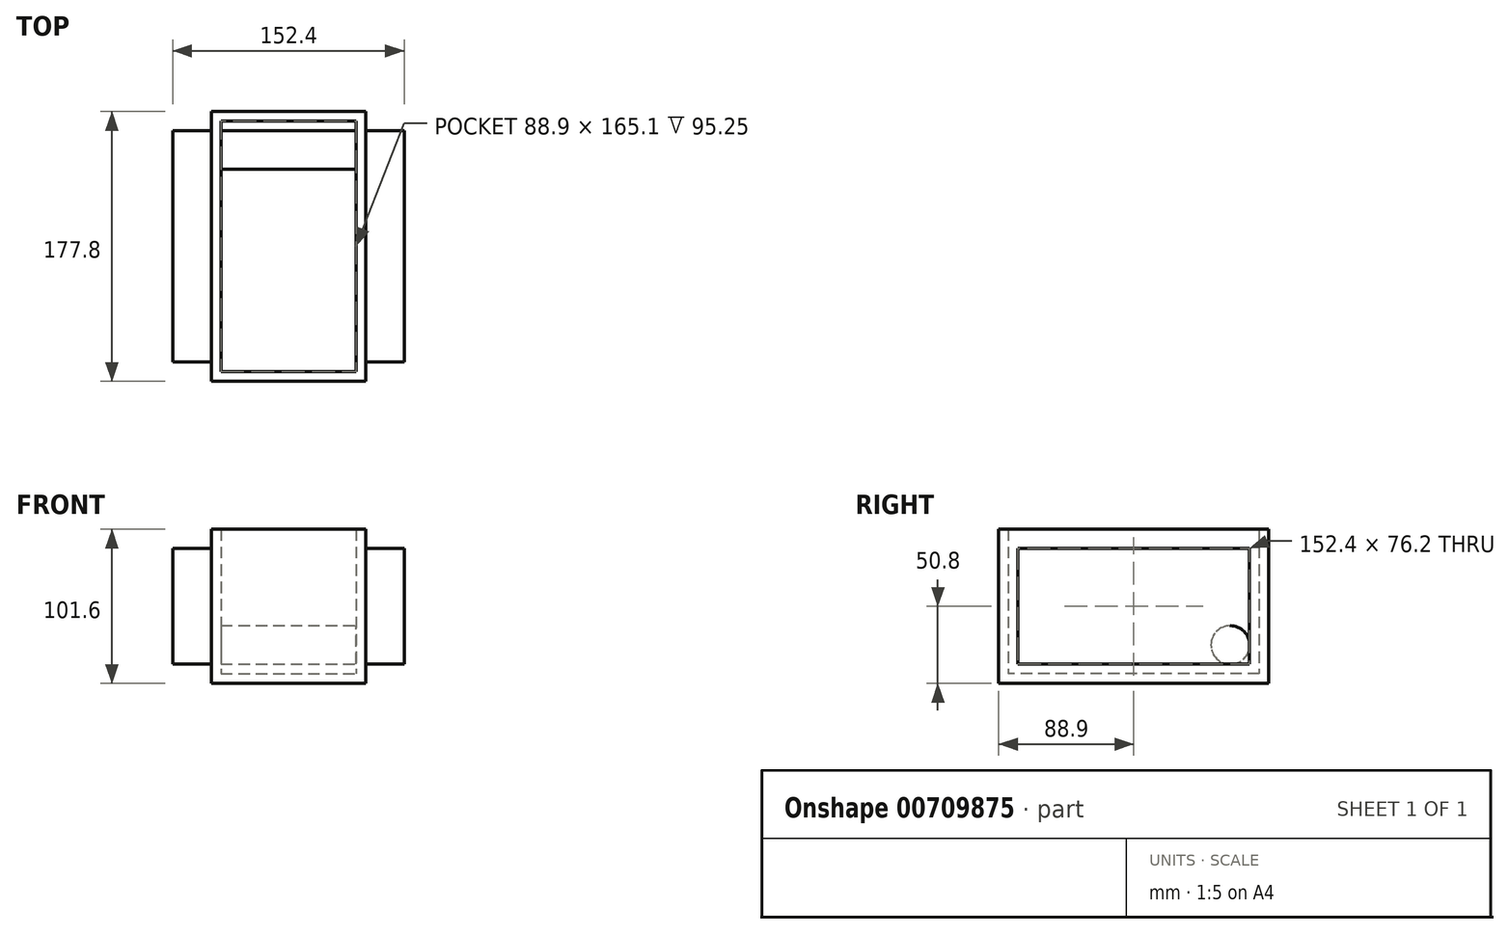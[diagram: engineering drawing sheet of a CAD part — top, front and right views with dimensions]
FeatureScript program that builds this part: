
annotation { "Feature Type Name" : "Feature", "Feature Type Description" : "" }
export const myFeature = defineFeature(function(context is Context, id is Id, definition is map)
    precondition{}
    {
        {
            var Q0;
            Q0=qCreatedBy(makeId("Top.planeOp"),FACE);
            var sketch = newSketch(context, id + "F0", { "sketchPlane" : qUnion([Q0])});
            skLineSegment(sketch, "E0.bottom", {"start": v(-50.8, 88.9) * mm, "end": v(50.8, 88.9) * mm});
            skLineSegment(sketch, "E0.top", {"start": v(-50.8, -88.9) * mm, "end": v(50.8, -88.9) * mm});
            skLineSegment(sketch, "E0.left", {"start": v(-50.8, 88.9) * mm, "end": v(-50.8, -88.9) * mm});
            skLineSegment(sketch, "E0.right", {"start": v(50.8, 88.9) * mm, "end": v(50.8, -88.9) * mm});
            skSolve(sketch);
        }
        {
            var Q0;
            Q0=makeQuery(id+"F0.imprint","IMPRINT",FACE,{"disambiguationData":[TD([[makeQuery(id+"F0.imprint","IMPRINT",EDGE,{"derivedFrom":sQuery(id+"F0.wireOp",EDGE,"E0.bottom")}),-1.0]])]});
            extrude(context, id + "F1", {"entities" : qUnion([Q0]), "endBound" : BoundingType.SYMMETRIC, "depth" : 101.6 * mm, "offsetDistance" : 25.4 * mm});
        }
        {
            var Q0;
            Q0=makeQuery(id+"F1.opExtrude","CAP_FACE",FACE,{"disambiguationData":[OSD([sQuery(id+"F0.wireOp",EDGE,"E0.bottom"),sQuery(id+"F0.wireOp",EDGE,"E0.top"),sQuery(id+"F0.wireOp",EDGE,"E0.left"),sQuery(id+"F0.wireOp",EDGE,"E0.right")])],"isStart":false});
            shell(context, id + "F2", {"entities" : qUnion([Q0]), "thickness" : 6.35 * mm});
        }
        {
            var Q0;
            Q0=makeQuery(id+"F1.opExtrude","SWEPT_FACE",FACE,{"disambiguationData":[OSD([sQuery(id+"F0.wireOp",EDGE,"E0.left")])]});
            var sketch = newSketch(context, id + "F3", { "sketchPlane" : qUnion([Q0])});
            skLineSegment(sketch, "E1.bottom", {"start": v(-76.2, 38.1) * mm, "end": v(76.2, 38.1) * mm});
            skLineSegment(sketch, "E1.top", {"start": v(-76.2, -38.1) * mm, "end": v(76.2, -38.1) * mm});
            skLineSegment(sketch, "E1.left", {"start": v(-76.2, 38.1) * mm, "end": v(-76.2, -38.1) * mm});
            skLineSegment(sketch, "E1.right", {"start": v(76.2, 38.1) * mm, "end": v(76.2, -38.1) * mm});
            skSolve(sketch);
        }
        {
            var Q0;
            Q0 = qSketchRegion(id + "F3", true);
            extrude(context, id + "F4", {"entities" : qUnion([Q0]), "operationType" : NewBodyOperationType.ADD, "depth" : 25.4 * mm, "offsetDistance" : 25.4 * mm});
        }
        {
            var Q0;
            Q0=makeQuery(id+"F1.opExtrude","SWEPT_FACE",FACE,{"disambiguationData":[OSD([sQuery(id+"F0.wireOp",EDGE,"E0.right")])]});
            var sketch = newSketch(context, id + "F5", { "sketchPlane" : qUnion([Q0])});
            skLineSegment(sketch, "E2.bottom", {"start": v(-76.2, 38.1) * mm, "end": v(76.2, 38.1) * mm});
            skLineSegment(sketch, "E2.top", {"start": v(-76.2, -38.1) * mm, "end": v(76.2, -38.1) * mm});
            skLineSegment(sketch, "E2.left", {"start": v(-76.2, 38.1) * mm, "end": v(-76.2, -38.1) * mm});
            skLineSegment(sketch, "E2.right", {"start": v(76.2, 38.1) * mm, "end": v(76.2, -38.1) * mm});
            skSolve(sketch);
        }
        {
            var Q0;
            Q0 = qSketchRegion(id + "F5", true);
            extrude(context, id + "F6", {"entities" : qUnion([Q0]), "operationType" : NewBodyOperationType.ADD, "depth" : 25.4 * mm, "offsetDistance" : 25.4 * mm});
        }
        {
            var Q0;
            Q0=makeQuery(id+"F2.opShell","OFFSET_FACE",FACE,{"disambiguationData":[OSD([sQuery(id+"F0.wireOp",EDGE,"E0.right")])]});
            var sketch = newSketch(context, id + "F7", { "sketchPlane" : qUnion([Q0])});
            skCircle(sketch, "E3", {"center": v(-63.5, -25.4) * mm, "radius": 12.7 * mm});
            skSolve(sketch);
        }
        {
            var Q0;
            Q0=makeQuery(id+"F7.imprint","IMPRINT",FACE,{"disambiguationData":[TD([[makeQuery(id+"F7.imprint","IMPRINT",EDGE,{"derivedFrom":sQuery(id+"F7.wireOp",EDGE,"E3")}),1.0]])]});
            extrude(context, id + "F8", {"entities" : qUnion([Q0]), "operationType" : NewBodyOperationType.ADD, "depth" : 88.9 * mm, "offsetDistance" : 25.4 * mm});
        }
    });
